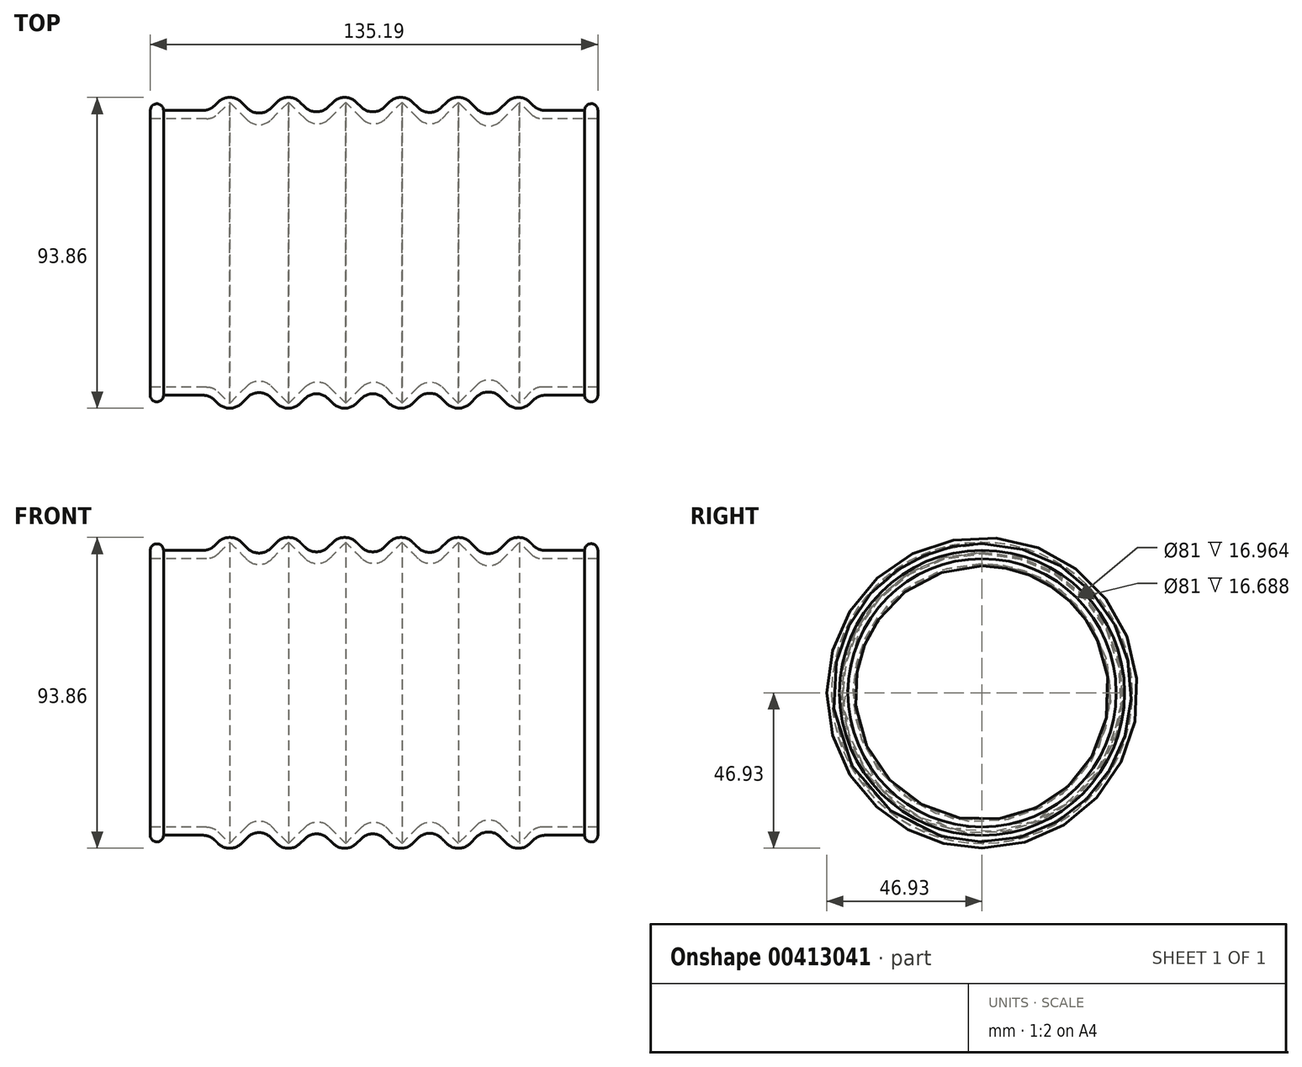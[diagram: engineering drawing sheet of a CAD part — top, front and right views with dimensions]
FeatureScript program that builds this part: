
annotation { "Feature Type Name" : "Feature", "Feature Type Description" : "" }
export const myFeature = defineFeature(function(context is Context, id is Id, definition is map)
    precondition{}
    {
        {
            var Q0;
            Q0=qCreatedBy(makeId("Front.planeOp"),FACE);
            var sketch = newSketch(context, id + "F0", { "sketchPlane" : qUnion([Q0])});
            skLineSegment(sketch, "E0", {"start": v(-53.23, 40.5) * mm, "end": v(-53.23, 43) * mm});
            skArc(sketch, "E1", {"start": v(-49.23, 43) * mm, "mid": v(-51.23, 45) * mm, "end": v(-53.23, 43) * mm});
            skPoint(sketch, "E1.second.point", {"position": v(-49.23, 43) * mm});
            skPoint(sketch, "E1.third.point", {"position": v(-50.93, 44.98) * mm});
            skLineSegment(sketch, "E2.trimOffspring", {"start": v(-49.23, 43) * mm, "end": v(-35.23, 43) * mm});
            skLineSegment(sketch, "E3", {"start": v(-35.23, 49.83) * mm, "end": v(-35.23, 35.64) * mm, "construction": true});
            skLineSegment(sketch, "E4", {"start": v(-25.46, 49) * mm, "end": v(-36.38, 49) * mm, "construction": true});
            skLineSegment(sketch, "E5", {"start": v(-35.23, 43) * mm, "end": v(-29.23, 49) * mm});
            skLineSegment(sketch, "E6.0", {"start": v(-33.47, 41.23) * mm, "end": v(-29.23, 45.46) * mm});
            skLineSegment(sketch, "E7", {"start": v(-33.47, 41.23) * mm, "end": v(-34.2, 40.5) * mm});
            skLineSegment(sketch, "E8", {"start": v(-18.93, 36.6) * mm, "end": v(-17.2, 36.6) * mm, "construction": true});
            skLineSegment(sketch, "E9", {"start": v(-29.23, 45.46) * mm, "end": v(-20.37, 36.6) * mm});
            skLineSegment(sketch, "E10.0", {"start": v(-27.82, 47.59) * mm, "end": v(-20.37, 40.13) * mm});
            skLineSegment(sketch, "E11", {"start": v(-27.82, 47.59) * mm, "end": v(-29.23, 49) * mm});
            skLineSegment(sketch, "E12", {"start": v(-20.37, 36.6) * mm, "end": v(-15.2, 41.76) * mm});
            skLineSegment(sketch, "E13.0", {"start": v(-20.37, 40.13) * mm, "end": v(-16.97, 43.53) * mm});
            skPoint(sketch, "E14", {"position": v(-20.37, 40.13) * mm});
            skLineSegment(sketch, "E15", {"start": v(64.77, 35.64) * mm, "end": v(64.77, 13.66) * mm, "construction": true});
            skLineSegment(sketch, "E16", {"start": v(82.77, 35.64) * mm, "end": v(82.77, 13.66) * mm, "construction": true});
            skLineSegment(sketch, "E17", {"start": v(-35.23, 30.4) * mm, "end": v(-35.23, 9.83) * mm, "construction": true});
            skLineSegment(sketch, "E18", {"start": v(-53.23, 36.6) * mm, "end": v(-53.23, 9.83) * mm, "construction": true});
            skLineSegment(sketch, "E19", {"start": v(-25.46, 49) * mm, "end": v(22.4, 49) * mm, "construction": true});
            skLineSegment(sketch, "E20", {"start": v(-29.23, 45.46) * mm, "end": v(33.33, 45.46) * mm, "construction": true});
            skLineSegment(sketch, "E21", {"start": v(-16.97, 43.53) * mm, "end": v(-11.5, 49) * mm});
            skLineSegment(sketch, "E22", {"start": v(-11.5, 49) * mm, "end": v(-3, 40.5) * mm});
            skLineSegment(sketch, "E23", {"start": v(-3, 40.5) * mm, "end": v(5.5, 49) * mm});
            skLineSegment(sketch, "E24", {"start": v(5.5, 49) * mm, "end": v(14, 40.5) * mm});
            skLineSegment(sketch, "E25", {"start": v(14, 40.5) * mm, "end": v(22.5, 49) * mm});
            skLineSegment(sketch, "E26", {"start": v(-15.2, 41.76) * mm, "end": v(-11.5, 45.46) * mm});
            skLineSegment(sketch, "E27", {"start": v(22.5, 49) * mm, "end": v(59.75, 49) * mm, "construction": true});
            skLineSegment(sketch, "E28", {"start": v(33.33, 45.46) * mm, "end": v(66.06, 45.46) * mm, "construction": true});
            skLineSegment(sketch, "E29", {"start": v(22.5, 49) * mm, "end": v(31.17, 40.33) * mm});
            skLineSegment(sketch, "E30", {"start": v(31.17, 40.33) * mm, "end": v(39.84, 49) * mm});
            skLineSegment(sketch, "E31", {"start": v(39.84, 49) * mm, "end": v(48.9, 39.94) * mm});
            skLineSegment(sketch, "E32", {"start": v(48.9, 39.94) * mm, "end": v(57.96, 49) * mm});
            skLineSegment(sketch, "E33", {"start": v(-11.5, 45.46) * mm, "end": v(-2.7, 36.93) * mm});
            skLineSegment(sketch, "E34", {"start": v(-2.7, 36.93) * mm, "end": v(5.8, 45.43) * mm});
            skLineSegment(sketch, "E35", {"start": v(5.8, 45.43) * mm, "end": v(14.3, 36.93) * mm});
            skLineSegment(sketch, "E36", {"start": v(14.3, 36.93) * mm, "end": v(22.8, 45.43) * mm});
            skLineSegment(sketch, "E37", {"start": v(22.8, 45.43) * mm, "end": v(31.3, 36.93) * mm});
            skLineSegment(sketch, "E38", {"start": v(49.08, 36.23) * mm, "end": v(58.27, 45.43) * mm});
            skLineSegment(sketch, "E39", {"start": v(63.96, 43) * mm, "end": v(57.96, 49) * mm});
            skLineSegment(sketch, "E40", {"start": v(58.27, 45.43) * mm, "end": v(63.2, 40.5) * mm});
            skLineSegment(sketch, "E41", {"start": v(63.2, 40.5) * mm, "end": v(81.96, 40.5) * mm});
            skLineSegment(sketch, "E42", {"start": v(63.96, 43) * mm, "end": v(77.96, 43) * mm});
            skLineSegment(sketch, "E43", {"start": v(81.96, 43.05) * mm, "end": v(81.96, 40.5) * mm});
            skPoint(sketch, "E44", {"position": v(79.96, 43.03) * mm});
            skArc(sketch, "E45", {"start": v(81.96, 43) * mm, "mid": v(79.96, 45.03) * mm, "end": v(77.96, 43) * mm});
            skLineSegment(sketch, "E46", {"start": v(39.84, 49) * mm, "end": v(39.84, 44.03) * mm, "construction": true});
            skPoint(sketch, "E47", {"position": v(39.84, 45.46) * mm});
            skLineSegment(sketch, "E48.0", {"start": v(39.84, 45.46) * mm, "end": v(49.08, 36.23) * mm});
            skLineSegment(sketch, "E49.0", {"start": v(31.3, 36.93) * mm, "end": v(39.84, 45.46) * mm});
            skLineSegment(sketch, "E50", {"start": v(-34.2, 40.5) * mm, "end": v(-53.23, 40.5) * mm});
            skSolve(sketch);
        }
        {
            var Q0;
            Q0=qCreatedBy(makeId("Front.planeOp"),FACE);
            var sketch = newSketch(context, id + "F1", { "sketchPlane" : qUnion([Q0])});
            skLineSegment(sketch, "E51", {"start": v(-68.83, 0) * mm, "end": v(93.36, 0) * mm});
            skSolve(sketch);
        }
        {
            var Q0;
            Q0 = qSketchRegion(id + "F1", true);
            var Q1;
            Q1=makeQuery(id+"F0.imprint","IMPRINT",FACE,{"disambiguationData":[TD([[makeQuery(id+"F0.imprint","IMPRINT",EDGE,{"derivedFrom":sQuery(id+"F0.wireOp",EDGE,"E0")}),-1.0]])]});
            var Q2;
            Q2=sQuery(id+"F1.wireOp",EDGE,"E51");
            revolve(context, id + "F2", {"entities" : qUnion([Q0, Q1]), "axis" : qUnion([Q2]), "revolveType" : RevolveType.FULL});
        }
        {
            var Q0;
            Q0=makeQuery(id+"F2.opRevolve","SWEPT_EDGE",EDGE,{"disambiguationData":[OSD([sQuery(id+"F0.wireOp",EDGE,"E2.trimOffspring"),sQuery(id+"F0.wireOp",EDGE,"E5")])]});
            var Q1;
            Q1=makeQuery(id+"F2.opRevolve","SWEPT_EDGE",EDGE,{"disambiguationData":[OSD([sQuery(id+"F0.wireOp",EDGE,"E5"),sQuery(id+"F0.wireOp",EDGE,"E11")])]});
            var Q2;
            Q2=makeQuery(id+"F2.opRevolve","SWEPT_EDGE",EDGE,{"disambiguationData":[OSD([sQuery(id+"F0.wireOp",EDGE,"E10.0"),sQuery(id+"F0.wireOp",EDGE,"E13.0")])]});
            var Q3;
            Q3=makeQuery(id+"F2.opRevolve","SWEPT_EDGE",EDGE,{"disambiguationData":[OSD([sQuery(id+"F0.wireOp",EDGE,"E21"),sQuery(id+"F0.wireOp",EDGE,"E22")])]});
            var Q4;
            Q4=makeQuery(id+"F2.opRevolve","SWEPT_EDGE",EDGE,{"disambiguationData":[OSD([sQuery(id+"F0.wireOp",EDGE,"E22"),sQuery(id+"F0.wireOp",EDGE,"E23")])]});
            var Q5;
            Q5=makeQuery(id+"F2.opRevolve","SWEPT_EDGE",EDGE,{"disambiguationData":[OSD([sQuery(id+"F0.wireOp",EDGE,"E23"),sQuery(id+"F0.wireOp",EDGE,"E24")])]});
            var Q6;
            Q6=makeQuery(id+"F2.opRevolve","SWEPT_EDGE",EDGE,{"disambiguationData":[OSD([sQuery(id+"F0.wireOp",EDGE,"E24"),sQuery(id+"F0.wireOp",EDGE,"E25")])]});
            var Q7;
            Q7=makeQuery(id+"F2.opRevolve","SWEPT_EDGE",EDGE,{"disambiguationData":[OSD([sQuery(id+"F0.wireOp",EDGE,"E25"),sQuery(id+"F0.wireOp",EDGE,"E29")])]});
            var Q8;
            Q8=makeQuery(id+"F2.opRevolve","SWEPT_EDGE",EDGE,{"disambiguationData":[OSD([sQuery(id+"F0.wireOp",EDGE,"E29"),sQuery(id+"F0.wireOp",EDGE,"E30")])]});
            var Q9;
            Q9=makeQuery(id+"F2.opRevolve","SWEPT_EDGE",EDGE,{"disambiguationData":[OSD([sQuery(id+"F0.wireOp",EDGE,"E30"),sQuery(id+"F0.wireOp",EDGE,"E31")])]});
            var Q10;
            Q10=makeQuery(id+"F2.opRevolve","SWEPT_EDGE",EDGE,{"disambiguationData":[OSD([sQuery(id+"F0.wireOp",EDGE,"E31"),sQuery(id+"F0.wireOp",EDGE,"E32")])]});
            var Q11;
            Q11=makeQuery(id+"F2.opRevolve","SWEPT_EDGE",EDGE,{"disambiguationData":[OSD([sQuery(id+"F0.wireOp",EDGE,"E32"),sQuery(id+"F0.wireOp",EDGE,"E39")])]});
            var Q12;
            Q12=makeQuery(id+"F2.opRevolve","SWEPT_EDGE",EDGE,{"disambiguationData":[OSD([sQuery(id+"F0.wireOp",EDGE,"E39"),sQuery(id+"F0.wireOp",EDGE,"E42")])]});
            fillet(context, id + "F3", {"entities" : qUnion([Q0, Q1, Q2, Q3, Q4, Q5, Q6, Q7, Q8, Q9, Q10, Q11, Q12]), "radius" : 5 * mm, "tangentPropagation" : true, "allowEdgeOverflow" : false});
        }
        {
            var Q0;
            Q0=makeQuery(id+"F2.opRevolve","SWEPT_EDGE",EDGE,{"disambiguationData":[OSD([sQuery(id+"F0.wireOp",EDGE,"E7"),sQuery(id+"F0.wireOp",EDGE,"E50")])]});
            fillet(context, id + "F4", {"entities" : qUnion([Q0]), "radius" : 5 * mm, "tangentPropagation" : true, "allowEdgeOverflow" : false});
        }
        {
            var Q0;
            {var subQ0=sQuery(id+"F0.wireOp",EDGE,"E50");Q0=makeQuery(id+"F4.opFillet","BLEND_EDGE",EDGE,{"blendedFrom":[makeQuery(id+"F2.opRevolve","SWEPT_EDGE",EDGE,{"disambiguationData":[OSD([sQuery(id+"F0.wireOp",EDGE,"E7"),subQ0])]}),makeQuery(id+"F2.opRevolve","SWEPT_FACE",FACE,{"disambiguationData":[OSD([subQ0])]})],"blendedInto":[makeQuery(id+"F2.opRevolve","SWEPT_FACE",FACE,{"disambiguationData":[OSD([subQ0])]})]});}
            var Q1;
            Q1=makeQuery(id+"F2.opRevolve","SWEPT_EDGE",EDGE,{"disambiguationData":[OSD([sQuery(id+"F0.wireOp",EDGE,"E9"),sQuery(id+"F0.wireOp",EDGE,"E12")])]});
            var Q2;
            Q2=makeQuery(id+"F2.opRevolve","SWEPT_EDGE",EDGE,{"disambiguationData":[OSD([sQuery(id+"F0.wireOp",EDGE,"E33"),sQuery(id+"F0.wireOp",EDGE,"E34")])]});
            var Q3;
            Q3=makeQuery(id+"F2.opRevolve","SWEPT_EDGE",EDGE,{"disambiguationData":[OSD([sQuery(id+"F0.wireOp",EDGE,"E35"),sQuery(id+"F0.wireOp",EDGE,"E36")])]});
            var Q4;
            Q4=makeQuery(id+"F2.opRevolve","SWEPT_EDGE",EDGE,{"disambiguationData":[OSD([sQuery(id+"F0.wireOp",EDGE,"E37"),sQuery(id+"F0.wireOp",EDGE,"E49.0")])]});
            var Q5;
            Q5=makeQuery(id+"F2.opRevolve","SWEPT_EDGE",EDGE,{"disambiguationData":[OSD([sQuery(id+"F0.wireOp",EDGE,"E38"),sQuery(id+"F0.wireOp",EDGE,"E48.0")])]});
            var Q6;
            Q6=makeQuery(id+"F2.opRevolve","SWEPT_EDGE",EDGE,{"disambiguationData":[OSD([sQuery(id+"F0.wireOp",EDGE,"E40"),sQuery(id+"F0.wireOp",EDGE,"E41")])]});
            fillet(context, id + "F5", {"entities" : qUnion([Q0, Q1, Q2, Q3, Q4, Q5, Q6]), "radius" : 5 * mm, "tangentPropagation" : true, "allowEdgeOverflow" : false});
        }
    });
